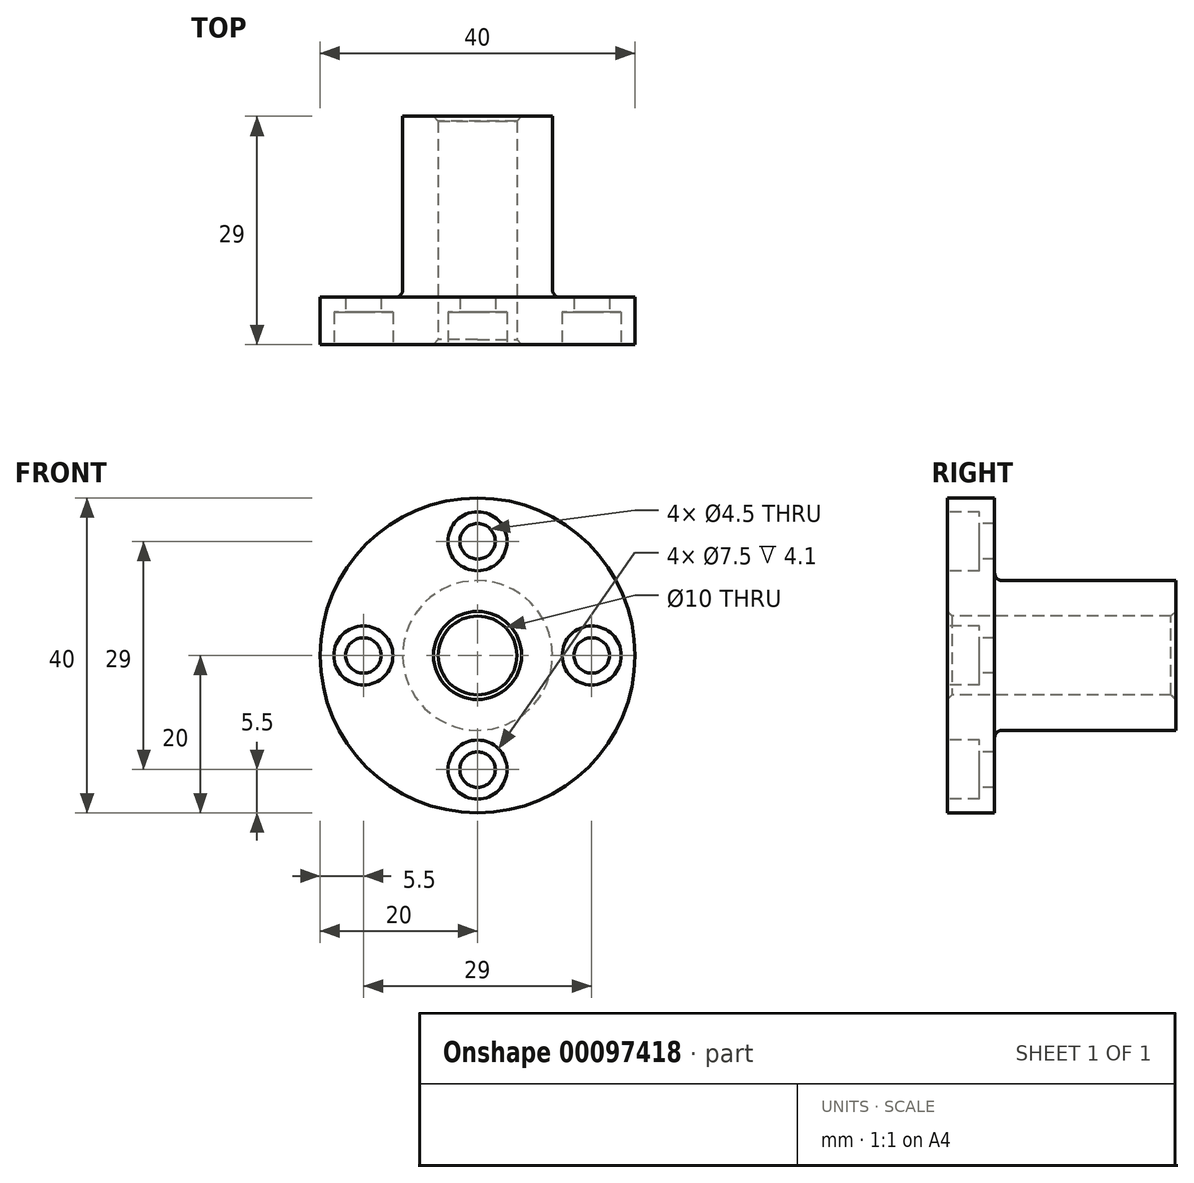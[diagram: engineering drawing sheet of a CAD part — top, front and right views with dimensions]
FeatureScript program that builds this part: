
annotation { "Feature Type Name" : "Feature", "Feature Type Description" : "" }
export const myFeature = defineFeature(function(context is Context, id is Id, definition is map)
    precondition{}
    {
        {
            var Q0;
            Q0=qCreatedBy(makeId("Top.planeOp"),FACE);
            var sketch = newSketch(context, id + "F0", { "sketchPlane" : qUnion([Q0])});
            skLineSegment(sketch, "E0", {"start": v(0, 0) * mm, "end": v(0, 23.73) * mm, "construction": true});
            skLineSegment(sketch, "E1", {"start": v(5, 0) * mm, "end": v(5, 29) * mm});
            skLineSegment(sketch, "E2", {"start": v(5, 29) * mm, "end": v(9.5, 29) * mm});
            skLineSegment(sketch, "E3", {"start": v(9.5, 29) * mm, "end": v(9.5, 6) * mm});
            skLineSegment(sketch, "E4", {"start": v(9.5, 6) * mm, "end": v(20, 6) * mm});
            skLineSegment(sketch, "E5", {"start": v(20, 6) * mm, "end": v(20, 0) * mm});
            skLineSegment(sketch, "E6", {"start": v(20, 0) * mm, "end": v(5, 0) * mm});
            skSolve(sketch);
        }
        {
            var Q0;
            Q0 = qSketchRegion(id + "F0", true);
            var Q1;
            Q1=makeQuery(id+"F0.imprint","IMPRINT",FACE,{"disambiguationData":[TD([[makeQuery(id+"F0.imprint","IMPRINT",EDGE,{"derivedFrom":sQuery(id+"F0.wireOp",EDGE,"E1")}),-1.0]])]});
            var Q2;
            Q2=sQuery(id+"F0.wireOp",EDGE,"E0");
            revolve(context, id + "F1", {"entities" : qUnion([Q0, Q1]), "axis" : qUnion([Q2]), "revolveType" : RevolveType.FULL});
        }
        {
            var Q0;
            Q0=makeQuery(id+"F1.opRevolve","SWEPT_FACE",FACE,{"disambiguationData":[OSD([sQuery(id+"F0.wireOp",EDGE,"E6")])]});
            var sketch = newSketch(context, id + "F2", { "sketchPlane" : qUnion([Q0])});
            skCircle(sketch, "E7", {"center": v(0, 0) * mm, "radius": 14.5 * mm, "construction": true});
            skCircle(sketch, "E8", {"center": v(0, 14.5) * mm, "radius": 2.25 * mm});
            skCircle(sketch, "E9", {"center": v(0, -14.5) * mm, "radius": 2.25 * mm});
            skCircle(sketch, "E10", {"center": v(14.5, 0) * mm, "radius": 2.25 * mm});
            skCircle(sketch, "E11", {"center": v(-14.5, 0) * mm, "radius": 2.25 * mm});
            skSolve(sketch);
        }
        {
            var Q0;
            Q0 = qSketchRegion(id + "F2", true);
            extrude(context, id + "F3", {"entities" : qUnion([Q0]), "operationType" : NewBodyOperationType.REMOVE, "endBound" : BoundingType.THROUGH_ALL, "oppositeDirection" : true, "depth" : 25 * mm});
        }
        {
            var Q0;
            Q0=makeQuery(id+"F1.opRevolve","SWEPT_FACE",FACE,{"disambiguationData":[OSD([sQuery(id+"F0.wireOp",EDGE,"E6")])]});
            var sketch = newSketch(context, id + "F4", { "sketchPlane" : qUnion([Q0])});
            skCircle(sketch, "E12", {"center": v(0, 14.5) * mm, "radius": 3.75 * mm});
            skCircle(sketch, "E13", {"center": v(14.5, 0) * mm, "radius": 3.75 * mm});
            skCircle(sketch, "E14", {"center": v(0, -14.5) * mm, "radius": 3.75 * mm});
            skCircle(sketch, "E15", {"center": v(-14.5, 0) * mm, "radius": 3.75 * mm});
            skSolve(sketch);
        }
        {
            var Q0;
            Q0 = qSketchRegion(id + "F4", true);
            extrude(context, id + "F5", {"entities" : qUnion([Q0]), "operationType" : NewBodyOperationType.REMOVE, "oppositeDirection" : true, "depth" : 4.1 * mm});
        }
        {
            var Q0;
            Q0=makeQuery(id+"F1.opRevolve","SWEPT_FACE",FACE,{"disambiguationData":[OSD([sQuery(id+"F0.wireOp",EDGE,"E1")])]});
            chamfer(context, id + "F6", {"entities" : qUnion([Q0]), "width" : 0.6 * mm, "tangentPropagation" : true});
        }
        {
            var Q0;
            Q0=makeQuery(id+"F1.opRevolve","SWEPT_EDGE",EDGE,{"disambiguationData":[OSD([sQuery(id+"F0.wireOp",EDGE,"E3"),sQuery(id+"F0.wireOp",EDGE,"E4")])]});
            fillet(context, id + "F7", {"entities" : qUnion([Q0]), "radius" : 1 * mm, "tangentPropagation" : true, "allowEdgeOverflow" : false});
        }
    });
